# Revit family: FU_Tablet_Sandler_Aryn Max Right ARX0160
name_source: partatom
category: Furniture
units: mm (PartAtom-declared; Revit-internal decimal feet)

## family parameters
Always vertical = Yes
Cut with Voids When Loaded = No
OmniClass Number = 23.40.20.00
OmniClass Title = General Furniture and Specialties
Room Calculation Point = No
Shared = No
Work Plane-Based = No

## types (1)
- ARYN MAX TABLET ARM FOR 4 LEGS BASE – RIGHT HAND
    Default Elevation = 0 mm  [stored 0 ft]
    Depth = 248 mm  [stored 0.813648 ft]
    Description = Optional detachable writing tablet for right-handed users. Fully foldable. Metal structure in chrome and joint in polished cast aluminum. For use with Aryn Max 4 leg frame chair.
    Height = 700 mm  [stored 2.29659 ft]
    Model = ARX0160
    URL = https://www.sandlerseating.com
    Width = 340 mm

note: [stored X ft] marks values corroborated as IEEE doubles in the binary element streams (Revit-internal decimal feet)

## geometry (parser evidence)
native form markers: Sweep x3
no freeform markers — native parametric forms only
